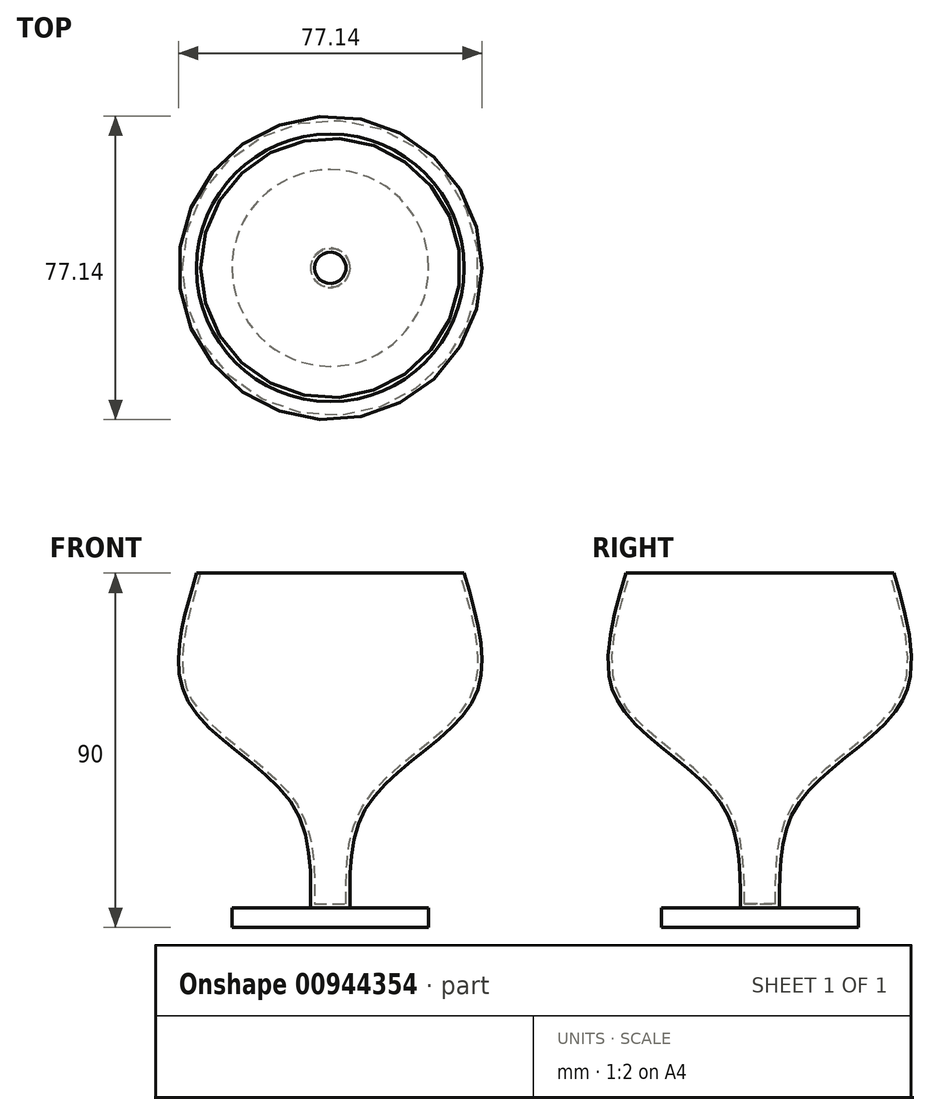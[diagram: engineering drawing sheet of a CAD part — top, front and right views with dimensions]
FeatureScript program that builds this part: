
annotation { "Feature Type Name" : "Feature", "Feature Type Description" : "" }
export const myFeature = defineFeature(function(context is Context, id is Id, definition is map)
    precondition{}
    {
        {
            var Q0;
            Q0=qCreatedBy(makeId("Top.planeOp"),FACE);
            var sketch = newSketch(context, id + "F0", { "sketchPlane" : qUnion([Q0])});
            skCircle(sketch, "E0", {"center": v(0, 0) * mm, "radius": 5 * mm});
            skSolve(sketch);
        }
        {
            var Q0;
            Q0=qCreatedBy(makeId("Top.planeOp"),FACE);
            cPlane(context, id + "F1", {"entities" : qUnion([Q0]), "cplaneType" : CPlaneType.OFFSET, "offset" : 85 * mm, "width" : 150 * mm, "height" : 150 * mm});
        }
        {
            var Q0;
            Q0=qCreatedBy(id+"F1.planeOp",FACE);
            var sketch = newSketch(context, id + "F2", { "sketchPlane" : qUnion([Q0])});
            skCircle(sketch, "E1", {"center": v(0, 0) * mm, "radius": 34 * mm});
            skSolve(sketch);
        }
        {
            var Q0;
            Q0=qCreatedBy(makeId("Top.planeOp"),FACE);
            cPlane(context, id + "F3", {"entities" : qUnion([Q0]), "cplaneType" : CPlaneType.OFFSET, "offset" : 24.7 * mm, "width" : 150 * mm, "height" : 150 * mm});
        }
        {
            var Q0;
            Q0=qCreatedBy(makeId("Top.planeOp"),FACE);
            cPlane(context, id + "F4", {"entities" : qUnion([Q0]), "cplaneType" : CPlaneType.OFFSET, "offset" : 54 * mm, "width" : 150 * mm, "height" : 150 * mm});
        }
        {
            var Q0;
            Q0=qCreatedBy(id+"F3.planeOp",FACE);
            var sketch = newSketch(context, id + "F5", { "sketchPlane" : qUnion([Q0])});
            skCircle(sketch, "E2", {"center": v(0, 0) * mm, "radius": 8.72 * mm});
            skSolve(sketch);
        }
        {
            var Q0;
            Q0=qCreatedBy(id+"F4.planeOp",FACE);
            var sketch = newSketch(context, id + "F6", { "sketchPlane" : qUnion([Q0])});
            skCircle(sketch, "E3", {"center": v(0, 0) * mm, "radius": 36.91 * mm});
            skSolve(sketch);
        }
        {
            var Q0;
            Q0=makeQuery(id+"F2.imprint","IMPRINT",FACE,{"disambiguationData":[TD([[makeQuery(id+"F2.imprint","IMPRINT",EDGE,{"derivedFrom":sQuery(id+"F2.wireOp",EDGE,"E1")}),1.0]])]});
            var Q1;
            Q1=makeQuery(id+"F6.imprint","IMPRINT",FACE,{"disambiguationData":[TD([[makeQuery(id+"F6.imprint","IMPRINT",EDGE,{"derivedFrom":sQuery(id+"F6.wireOp",EDGE,"E3")}),1.0]])]});
            var Q2;
            Q2=makeQuery(id+"F5.imprint","IMPRINT",FACE,{"disambiguationData":[TD([[makeQuery(id+"F5.imprint","IMPRINT",EDGE,{"derivedFrom":sQuery(id+"F5.wireOp",EDGE,"E2")}),1.0]])]});
            var Q3;
            Q3=makeQuery(id+"F0.imprint","IMPRINT",FACE,{"disambiguationData":[TD([[makeQuery(id+"F0.imprint","IMPRINT",EDGE,{"derivedFrom":sQuery(id+"F0.wireOp",EDGE,"E0")}),1.0]])]});
            loft(context, id + "F7", {"sheetProfilesArray" : [{ "sheetProfileEntities" : qUnion([Q0]) }, { "sheetProfileEntities" : qUnion([Q1]) }, { "sheetProfileEntities" : qUnion([Q2]) }, { "sheetProfileEntities" : qUnion([Q3]) }]});
        }
        {
            var Q0;
            Q0=makeQuery(id+"F7.opLoft","CAP_FACE",FACE,{"disambiguationData":[OSD([makeQuery(id+"F2.imprint","IMPRINT",FACE,{"disambiguationData":[TD([[makeQuery(id+"F2.imprint","IMPRINT",EDGE,{"derivedFrom":sQuery(id+"F2.wireOp",EDGE,"E1")}),1.0]])]})])],"isStart":true});
            shell(context, id + "F8", {"entities" : qUnion([Q0]), "thickness" : 1 * mm});
        }
        {
            var Q0;
            Q0=makeQuery(id+"F7.opLoft","CAP_FACE",FACE,{"disambiguationData":[OSD([makeQuery(id+"F0.imprint","IMPRINT",FACE,{"disambiguationData":[TD([[makeQuery(id+"F0.imprint","IMPRINT",EDGE,{"derivedFrom":sQuery(id+"F0.wireOp",EDGE,"E0")}),1.0]])]})])],"isStart":true});
            var sketch = newSketch(context, id + "F9", { "sketchPlane" : qUnion([Q0])});
            skCircle(sketch, "E4", {"center": v(0, 0) * mm, "radius": 5 * mm});
            skSolve(sketch);
        }
        {
            var Q0;
            Q0=makeQuery(id+"F9.imprint","IMPRINT",FACE,{"disambiguationData":[TD([[makeQuery(id+"F9.imprint","IMPRINT",EDGE,{"derivedFrom":sQuery(id+"F9.wireOp",EDGE,"E4")}),1.0]])]});
            var sketch = newSketch(context, id + "F10", { "sketchPlane" : qUnion([Q0])});
            skCircle(sketch, "E5", {"center": v(0, 0) * mm, "radius": 25 * mm});
            skSolve(sketch);
        }
        {
            var Q0;
            Q0 = qSketchRegion(id + "F10", true);
            extrude(context, id + "F11", {"entities" : qUnion([Q0]), "operationType" : NewBodyOperationType.ADD, "depth" : 5 * mm, "offsetDistance" : 25 * mm});
        }
    });
